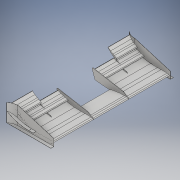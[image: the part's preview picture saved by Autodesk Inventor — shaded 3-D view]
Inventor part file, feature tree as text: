
AUTODESK INVENTOR PART (.ipt)
format: ipt  version: 2018.2 (Build 222227000, 227)  size: 917,504 bytes
history: native  units: mm
features: extrude x16, sketch x16, projected_geometry x11, other x4, chamfer x1, mirror x1
ambient origin geometry x8: Origin, YZ Plane, XZ Plane, XY Plane, X Axis, Y Axis, Z Axis, Center Point
bodies: Body1 (feature_tree)
feature tree (49):
  extrude  "押し出し7"  Depth=394.0mm TaperAngle=0.0deg
  extrude  "押し出し8"  Depth=5.0mm TaperAngle=0.0deg
  extrude  "押し出し9"  Depth=225.0mm TaperAngle=0.0deg
  extrude  "押し出し10"  Depth=5.0mm TaperAngle=0.0deg
  extrude  "押し出し11"  Depth=225.0mm TaperAngle=0.0deg
  extrude  "押し出し13"  Depth=2.0mm
  other  "厚み1"
  other  "厚み2"
  chamfer  "面取り1"  Distance=5.0mm
  extrude  "押し出し16"  Depth=225.0mm TaperAngle=0.0deg
  extrude  "押し出し17"  Depth=1.0mm
  extrude  "押し出し18"  Depth=1.0mm
  extrude  "押し出し20"  Depth=2.0mm
  extrude  "押し出し21"  Depth=2.0mm TaperAngle=45.0deg
  extrude  "押し出し22"  Depth=10.0mm TaperAngle=0.0deg
  extrude  "押し出し23"  Depth=5.0mm
  other  "面を削除1"
  extrude  "押し出し25"  Depth=2.0mm
  extrude  "押し出し27"  TaperAngle=0.0deg  [1 undecoded]
  extrude  "押し出し28"  Depth=35.0mm TaperAngle=0.0deg
  mirror  "ミラー7"
  other  "ソリッド36"
  sketch  "スケッチ8"
  projected_geometry  "投影ループ7"
  sketch  "スケッチ9"
  projected_geometry  "投影ループ8"
  sketch  "スケッチ10"
  projected_geometry  "投影ループ9"
  projected_geometry  "投影ループ10"
  sketch  "スケッチ11"
  projected_geometry  "投影ループ11"
  sketch  "スケッチ12"
  projected_geometry  "投影ループ12"
  projected_geometry  "投影ループ13"
  projected_geometry  "投影ループ14"
  sketch  "スケッチ14"
  projected_geometry  "投影ループ16"
  sketch  "スケッチ18"
  sketch  "スケッチ19"
  sketch  "スケッチ20"
  sketch  "スケッチ21"
  sketch  "スケッチ22"
  sketch  "スケッチ23"
  projected_geometry  "投影ループ18"
  sketch  "スケッチ24"
  projected_geometry  "投影ループ19"
  sketch  "スケッチ26"
  sketch  "スケッチ27"
  sketch  "スケッチ29"
note: 1 required parameter value undecoded (feature->parameter linkage not recoverable at this tier; creation-order binding heuristic only, values carry confidence <= 0.55)
